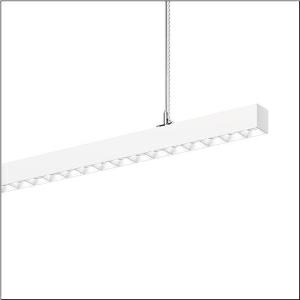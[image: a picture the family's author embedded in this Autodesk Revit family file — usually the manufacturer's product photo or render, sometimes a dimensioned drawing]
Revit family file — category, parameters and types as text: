
# Revit family: silica_r__21_51mx36dc4dwb_53ae
name_source: partatom
category: Lighting Fixtures
units: mm (PartAtom-declared; Revit-internal decimal feet)

## family parameters
Cut with Voids When Loaded = No
Host = Face
Light Source = No
Part Type = Normal
Room Calculation Point = No
Round Connector Dimension = Use Diameter
Shared = No

## types (1)
- --- (1 x LED, 17650 lm, 97.4 W, 4000K)
    Apparent Load = 97 VA
    CIE Flux Codes = 83 98 100 61 100
    Color Rendering = 80
    Color Temperature = 4000K
    Default Elevation = 1800 mm
    Description = Silica® 21, office luminaire, primary light control with darklight reflector, of PMMA, white, CAT 2 (L<= 3000cd/m²), light emission: direct/indirect distribution, primary light characteristic: symmetric, installation type: suspended mounting, LED, rated luminous flux: 17.650lm, luminous efficacy: 181lm/W, light colour: 840, colour temperature: 4000K, with terminal, 3+2-pole, max. 2.5mm², mains connection: 220..240V, AC, 50/60Hz, rated input power: 97.4W, luminaire housing, of aluminium, traffic white (RAL 9016), length: 3.004mm, width: 53mm, height: 53mm, protection rating (complete): IP20, insulation class (complete): insulation class I (protective earthing), certification: CE, permissible operating ambient temperature: 0..+35°C, standard: EN 50419, packaging unit: 1 piece
    Height = 53 mm
    Lamp = 1 x LED
    Lamp Light Flux = 17650 lm
    Lamp Power = 97.4 W
    Lamp count = 1
    Length = 3004 mm
    Luminous efficacy = 181 lm/W
    Manufacturer = Siteco
    ModVariant = No
    Model = 51MX36DC4DWB
    Mounting Place = Ceiling
    Mounting Type = Pendant
    Number of Poles = 1
    OnlyDefault = Yes
    Power Factor = 1
    Product Name = Silica® 21
    Product group = office luminaire | ceiling pendant
    ProductGroupID = 902
    Protection Class = Protection class I
    Protection Degree = IP 20
    RLX_Detail_Level = 1
    RLX_Emergency_Light_Flux = 0 lm
    RLX_Emergency_Type = 0
    RLX_Emergency_Type_DB = No
    RlxData = <blob elided: 61317 chars, md5=a16334eb>
    Socket = socket
    Standby Power = 0 W
    System Light Flux = 17650 lm
    System Power = 97 W
    Type Comments = factory setting: luminous flux: 100 % | dim-lin: 254 | 336 mA
    Type Image = l_1297797.jpg
    URL = http://relux.com
    VarID = @adj_052175
    Voltage = 0 V
    Weight = 0.00 kg
    Width = 53 mm

## geometry (parser evidence)
native form markers: Blend x4, Sweep x12
no freeform markers — native parametric forms only
